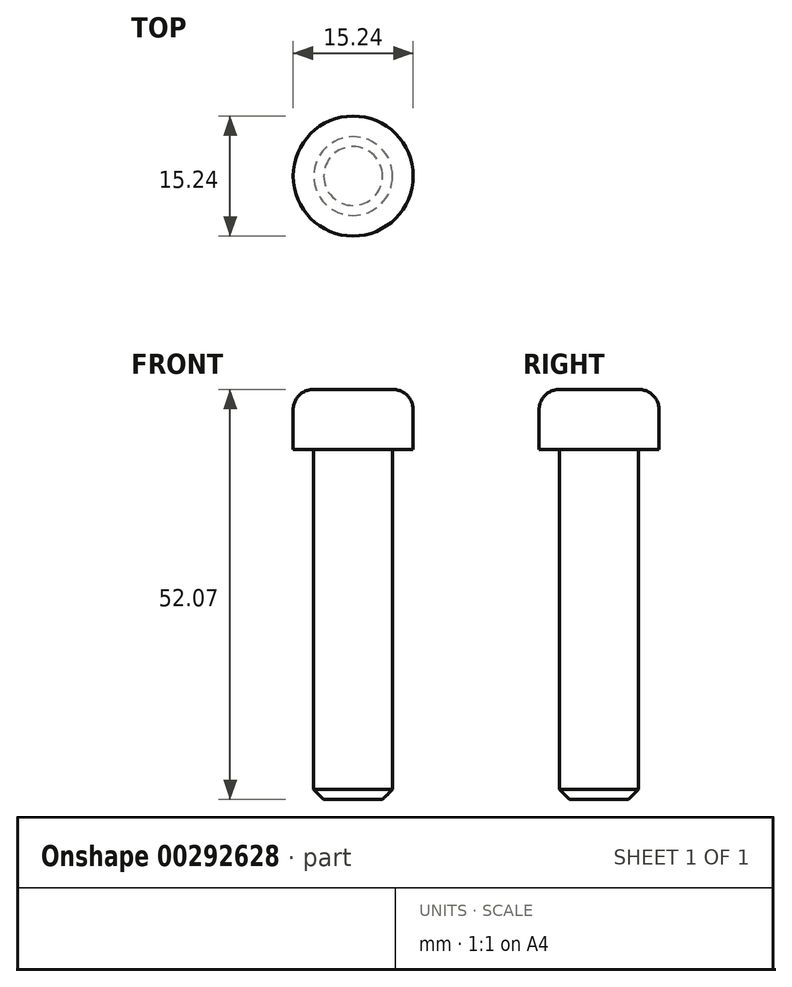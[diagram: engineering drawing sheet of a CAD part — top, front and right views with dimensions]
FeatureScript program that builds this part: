
annotation { "Feature Type Name" : "Feature", "Feature Type Description" : "" }
export const myFeature = defineFeature(function(context is Context, id is Id, definition is map)
    precondition{}
    {
        {
            var Q0;
            Q0=qCreatedBy(makeId("Top.planeOp"),FACE);
            var sketch = newSketch(context, id + "F0", { "sketchPlane" : qUnion([Q0])});
            skCircle(sketch, "E0", {"center": v(0, 0) * mm, "radius": 5 * mm});
            skSolve(sketch);
        }
        {
            var Q0;
            Q0=makeQuery(id+"F0.imprint","IMPRINT",FACE,{"disambiguationData":[TD([[makeQuery(id+"F0.imprint","IMPRINT",EDGE,{"derivedFrom":sQuery(id+"F0.wireOp",EDGE,"E0")}),1.0]])]});
            extrude(context, id + "F1", {"entities" : qUnion([Q0]), "depth" : 44.45 * mm});
        }
        {
            var Q0;
            Q0=makeQuery(id+"F1.opExtrude","CAP_FACE",FACE,{"disambiguationData":[OSD([sQuery(id+"F0.wireOp",EDGE,"E0")])],"isStart":false});
            var sketch = newSketch(context, id + "F2", { "sketchPlane" : qUnion([Q0])});
            skCircle(sketch, "E1", {"center": v(0, 0) * mm, "radius": 7.62 * mm});
            skSolve(sketch);
        }
        {
            var Q0;
            Q0=makeQuery(id+"F2.imprint","IMPRINT",FACE,{"disambiguationData":[TD([[makeQuery(id+"F2.imprint","IMPRINT",EDGE,{"derivedFrom":sQuery(id+"F2.wireOp",EDGE,"E1")}),1.0]])]});
            var Q1;
            Q1=makeQuery(id+"F2.imprint","IMPRINT",FACE,{"disambiguationData":[TD([[makeQuery(id+"F2.imprint","IMPRINT",EDGE,{"derivedFrom":makeQuery(id+"F1.opExtrude","CAP_EDGE",EDGE,{"disambiguationData":[OSD([sQuery(id+"F0.wireOp",EDGE,"E0")])],"isStart":false})}),1.0]])]});
            extrude(context, id + "F3", {"entities" : qUnion([Q0, Q1]), "operationType" : NewBodyOperationType.ADD, "depth" : 7.62 * mm});
        }
        {
            var Q0;
            Q0=makeQuery(id+"F3.opExtrude","CAP_EDGE",EDGE,{"disambiguationData":[OSD([sQuery(id+"F2.wireOp",EDGE,"E1")])],"isStart":false});
            fillet(context, id + "F4", {"entities" : qUnion([Q0]), "radius" : 2.54 * mm, "tangentPropagation" : true, "allowEdgeOverflow" : false});
        }
        {
            var Q0;
            Q0=makeQuery(id+"F1.opExtrude","CAP_EDGE",EDGE,{"disambiguationData":[OSD([sQuery(id+"F0.wireOp",EDGE,"E0")])],"isStart":true});
            chamfer(context, id + "F5", {"entities" : qUnion([Q0]), "width" : 1.27 * mm, "tangentPropagation" : true});
        }
    });
